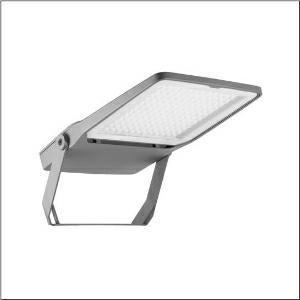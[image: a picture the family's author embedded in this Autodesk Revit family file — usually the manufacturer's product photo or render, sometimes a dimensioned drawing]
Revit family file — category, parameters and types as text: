
# Revit family: floodlight_fl_20_midi___pl52_5xa7681d2d1ac_0834
name_source: partatom
category: Lighting Fixtures
units: mm (PartAtom-declared; Revit-internal decimal feet)

## family parameters
Cut with Voids When Loaded = No
Host = Face
Light Source = No
Part Type = Normal
Room Calculation Point = No
Round Connector Dimension = Use Diameter
Shared = No

## types (1)
- Floodlight FL 20 midi  PL52 (1 x LED 4000K / CRI = 70 (unbekannt), 17990 lm, 4000K)
    Apparent Load = 142 VA
    CIE Flux Codes = 27 59 98 100 100
    Color Rendering = 70
    Color Temperature = 4000K
    Default Elevation = 1800 mm
    Description = Floodlight FL 20 midi, floodlight, primary light control with lens, of plastic, primary optical cover: protective disc, of toughened safety glass, transparent, light distribution: PL52, light emission: direct distribution, primary light characteristic: asymmetric, installation type: surface-mounted, LED High Power LED, rated luminous flux: 17.990 lm, light colour: 740, colour temperature: 4000K, control gear: ECG Basic, control: power reduction, overheat protection, electronic power reduction, with terminal, 5-pole, max. 2.5mm², mains connection: 220..240V, AC, 50/60Hz, rated input power: 142W, LED unit, of diecast aluminium, powder-coated, Siteco® metallic grey (DB 702S), length: 654 mm, width: 450 mm, height: 76mm, housing frame, of diecast aluminium, powder-coated, Siteco® metallic grey (DB 702S), mounting bracket, of steel, powder-coated, Siteco® metallic grey (DB 702S), ON/OFFprotection rating (complete): IP66, insulation class (complete): insulation class I (protective earthing), certification: CE, ENEC, VDE, protection symbol: D, permissible ambient temperature for indoor applications: -40..+40°C, permissible ambient temperature for outdoor applications: -40..+50°C, standard: DIN EN 12944, packaging unit: 1 piece

Light Distribution: PL52
    Height = 76 mm
    Lamp = 1 x LED 4000K / CRI >= 70 (unbekannt)
    Lamp Light Flux = 17990 lm
    Lamp count = 1
    Length = 672 mm
    Luminous efficacy = 127 lm/W
    Manufacturer = Siteco
    ModVariant = No
    Model = 5XA7681D2D1AC
    Number of Poles = 1
    OnlyDefault = Yes
    Power Factor = 1
    Product Name = Floodlight FL 20 midi | PL52
    Product group = floodlight | pylon top
    ProductGroupID = 6101
    Protection Class = Protection class I
    Protection Degree = IP 66
    RLX_Detail_Level = 1
    RlxData = <blob elided: 94149 chars, md5=0236fe5d>
    Socket = socket
    Standby Power = 0 W
    System Light Flux = 17990 lm
    System Power = 142 W
    Type Comments = Product without accessories
    Type Image = l_1005943.jpg
    URL = http://relux.com
    VarID = ---
    Voltage = 0 V
    Weight = 0.00 kg
    Width = 450 mm

## geometry (parser evidence)
native form markers: Blend x4, Sweep x14
no freeform markers — native parametric forms only
